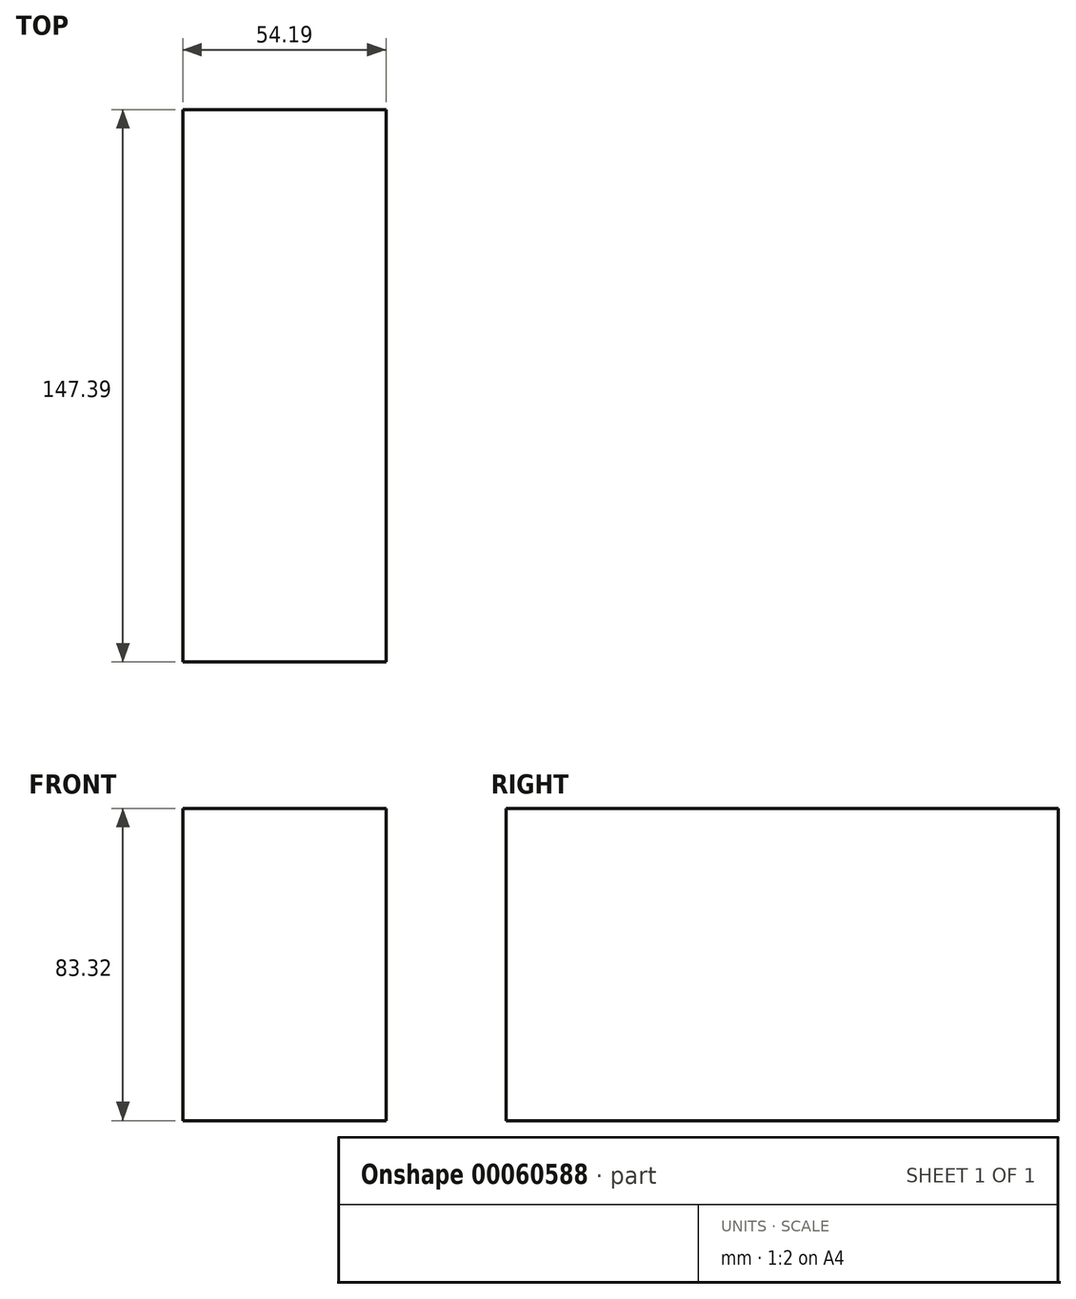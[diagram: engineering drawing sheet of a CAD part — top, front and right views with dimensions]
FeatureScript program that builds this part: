
annotation { "Feature Type Name" : "Feature", "Feature Type Description" : "" }
export const myFeature = defineFeature(function(context is Context, id is Id, definition is map)
    precondition{}
    {
        {
            var Q0;
            Q0=qCreatedBy(makeId("Front.planeOp"),FACE);
            var sketch = newSketch(context, id + "F1", { "sketchPlane" : qUnion([Q0])});
            skLineSegment(sketch, "E0.bottom", {"start": v(0, 0) * mm, "end": v(0, 0) * mm});
            skLineSegment(sketch, "E0.top", {"start": v(0, 0) * mm, "end": v(0, 0) * mm});
            skLineSegment(sketch, "E0.left", {"start": v(0, 0) * mm, "end": v(0, 0) * mm});
            skLineSegment(sketch, "E0.right", {"start": v(0, 0) * mm, "end": v(0, 0) * mm});
            skLineSegment(sketch, "E1.bottom", {"start": v(-54.19, 0) * mm, "end": v(0, 0) * mm});
            skLineSegment(sketch, "E1.top", {"start": v(-54.19, 83.32) * mm, "end": v(0, 83.32) * mm});
            skLineSegment(sketch, "E1.left", {"start": v(-54.19, 0) * mm, "end": v(-54.19, 83.32) * mm});
            skLineSegment(sketch, "E1.right", {"start": v(0, 0) * mm, "end": v(0, 83.32) * mm});
            skSolve(sketch);
        }
        {
            var Q0;
            Q0=makeQuery(id+"F1.imprint","IMPRINT",FACE,{"disambiguationData":[TD([[makeQuery(id+"F1.imprint","IMPRINT",EDGE,{"derivedFrom":sQuery(id+"F1.wireOp",EDGE,"E1.bottom")}),1.0]])]});
            extrude(context, id + "F0", {"entities" : qUnion([Q0]), "depth" : 147.4 * mm});
        }
    });
